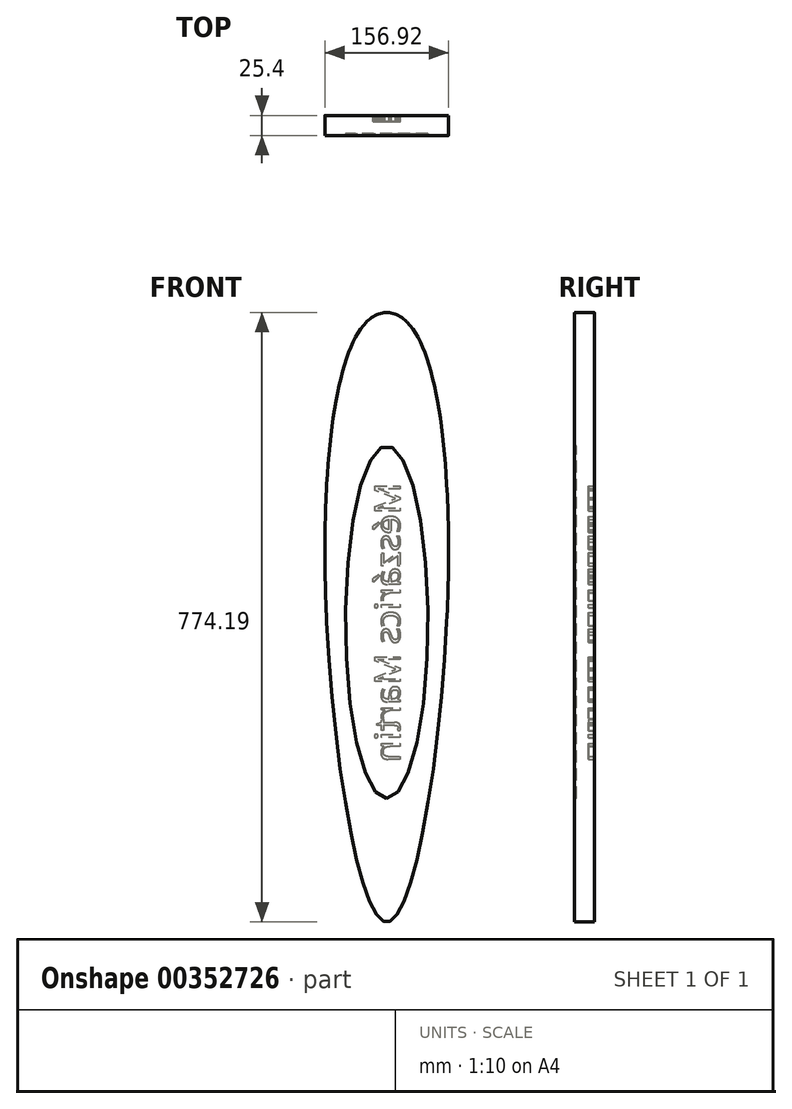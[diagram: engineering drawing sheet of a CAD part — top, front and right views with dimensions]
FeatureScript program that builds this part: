
annotation { "Feature Type Name" : "Feature", "Feature Type Description" : "" }
export const myFeature = defineFeature(function(context is Context, id is Id, definition is map)
    precondition{}
    {
        {
            var Q0;
            Q0=qCreatedBy(makeId("Front.planeOp"),FACE);
            var sketch = newSketch(context, id + "F0", { "sketchPlane" : qUnion([Q0])});
            skLineSegment(sketch, "E0.bottom", {"start": v(26, 381) * mm, "end": v(25.4, 381) * mm});
            skLineSegment(sketch, "E0.left", {"start": v(76.2, 174.95) * mm, "end": v(76.2, 0) * mm});
            skLineSegment(sketch, "E0.right", {"start": v(-76.2, 174.95) * mm, "end": v(-76.2, 0) * mm});
            skPoint(sketch, "E0.middle", {"position": v(0, 0) * mm});
            skLineSegment(sketch, "E1", {"start": v(0, 0) * mm, "end": v(0, 0) * mm});
            skPoint(sketch, "E1.endSnap0", {"position": v(0, 381) * mm});
            skLineSegment(sketch, "E2.bottom", {"start": v(25.4, 305.4) * mm, "end": v(-25.4, 305.4) * mm});
            skLineSegment(sketch, "E2.left", {"start": v(25.4, 305.4) * mm, "end": v(25.4, 381.6) * mm});
            skLineSegment(sketch, "E2.right", {"start": v(-25.4, 305.4) * mm, "end": v(-25.4, 381.6) * mm});
            skPoint(sketch, "E2.middle", {"position": v(0, 343.5) * mm});
            skLineSegment(sketch, "E3", {"start": v(0, 381) * mm, "end": v(0, 0) * mm, "construction": true});
            skLineSegment(sketch, "E4.trimOffspring", {"start": v(-25.4, 381) * mm, "end": v(-26, 381) * mm});
            skPoint(sketch, "E5.1.internal.orphan", {"position": v(76.2, 0) * mm});
            skPoint(sketch, "E5.2.internal.orphan", {"position": v(0, -381) * mm});
            skPoint(sketch, "E5.3.internal.orphan", {"position": v(-76.2, 0) * mm});
            skLineSegment(sketch, "E6", {"start": v(0, 0) * mm, "end": v(0, -381) * mm, "construction": true});
            skFitSpline(sketch, "E7", {"points": [v(25.4, 381.6) * mm, v(76.2, 0) * mm, v(0, -381) * mm, v(-76.2, 0) * mm, v(-25.4, 381.6) * mm, v(25.4, 381.6) * mm]});
            skPoint(sketch, "E8.orphan", {"position": v(-76.2, 381) * mm});
            skPoint(sketch, "E9.orphan", {"position": v(76.2, 381) * mm});
            skPoint(sketch, "E10.orphan", {"position": v(-76.2, -381) * mm});
            skSolve(sketch);
        }
        {
            var Q0;
            Q0=qSketchRegion(id+"F0",true);
            extrude(context, id + "F1", {"entities" : qUnion([Q0]), "depth" : 25.4 * mm});
        }
        {
            var Q0;
            Q0=makeQuery(id+"F1.opExtrude","CAP_FACE",FACE,{"disambiguationData":[OSD([sQuery(id+"F0.wireOp",EDGE,"E2.bottom"),sQuery(id+"F0.wireOp",EDGE,"E2.left"),sQuery(id+"F0.wireOp",EDGE,"E2.right"),sQuery(id+"F0.wireOp",EDGE,"E7")])],"isStart":false});
            var sketch = newSketch(context, id + "F2", { "sketchPlane" : qUnion([Q0])});
            skEllipse(sketch, "E11", {"center": v(0, 0) * mm, "majorRadius": 223.98 * mm, "minorRadius": 52.4 * mm, "majorAxis": v(0, -1)});
            skSolve(sketch);
        }
        {
            var Q0;
            Q0=qSketchRegion(id+"F2",true);
            extrude(context, id + "F3", {"entities" : qUnion([Q0]), "operationType" : NewBodyOperationType.REMOVE, "oppositeDirection" : true, "depth" : 2.54 * mm});
        }
        {
            var Q0;
            Q0=makeQuery(id+"F1.opExtrude","CAP_FACE",FACE,{"disambiguationData":[OSD([sQuery(id+"F0.wireOp",EDGE,"E2.bottom"),sQuery(id+"F0.wireOp",EDGE,"E2.left"),sQuery(id+"F0.wireOp",EDGE,"E2.right"),sQuery(id+"F0.wireOp",EDGE,"E7")])],"isStart":true});
            cPlane(context, id + "F4", {"entities" : qUnion([Q0]), "cplaneType" : CPlaneType.OFFSET, "offset" : 25.4 * mm, "width" : 152.4 * mm, "height" : 152.4 * mm});
        }
        {
            var Q0;
            Q0=qCreatedBy(id+"F4.planeOp",FACE);
            var sketch = newSketch(context, id + "F5", { "sketchPlane" : qUnion([Q0])});
            skText(sketch, "E12", { "text": "Mészárics Martin", "fontName": "OpenSans-Regular.ttf"});
            const initialGuessF5  = {"E12": [-0.01701, 0.17717, 0, -1, 0.03225]};
            skSetInitialGuess(sketch, initialGuessF5);
            skSolve(sketch);
        }
        {
            var Q0;
            Q0=qSketchRegion(id+"F5",true);
            extrude(context, id + "F6", {"entities" : qUnion([Q0]), "operationType" : NewBodyOperationType.REMOVE, "oppositeDirection" : true, "depth" : 33.02 * mm});
        }
    });
